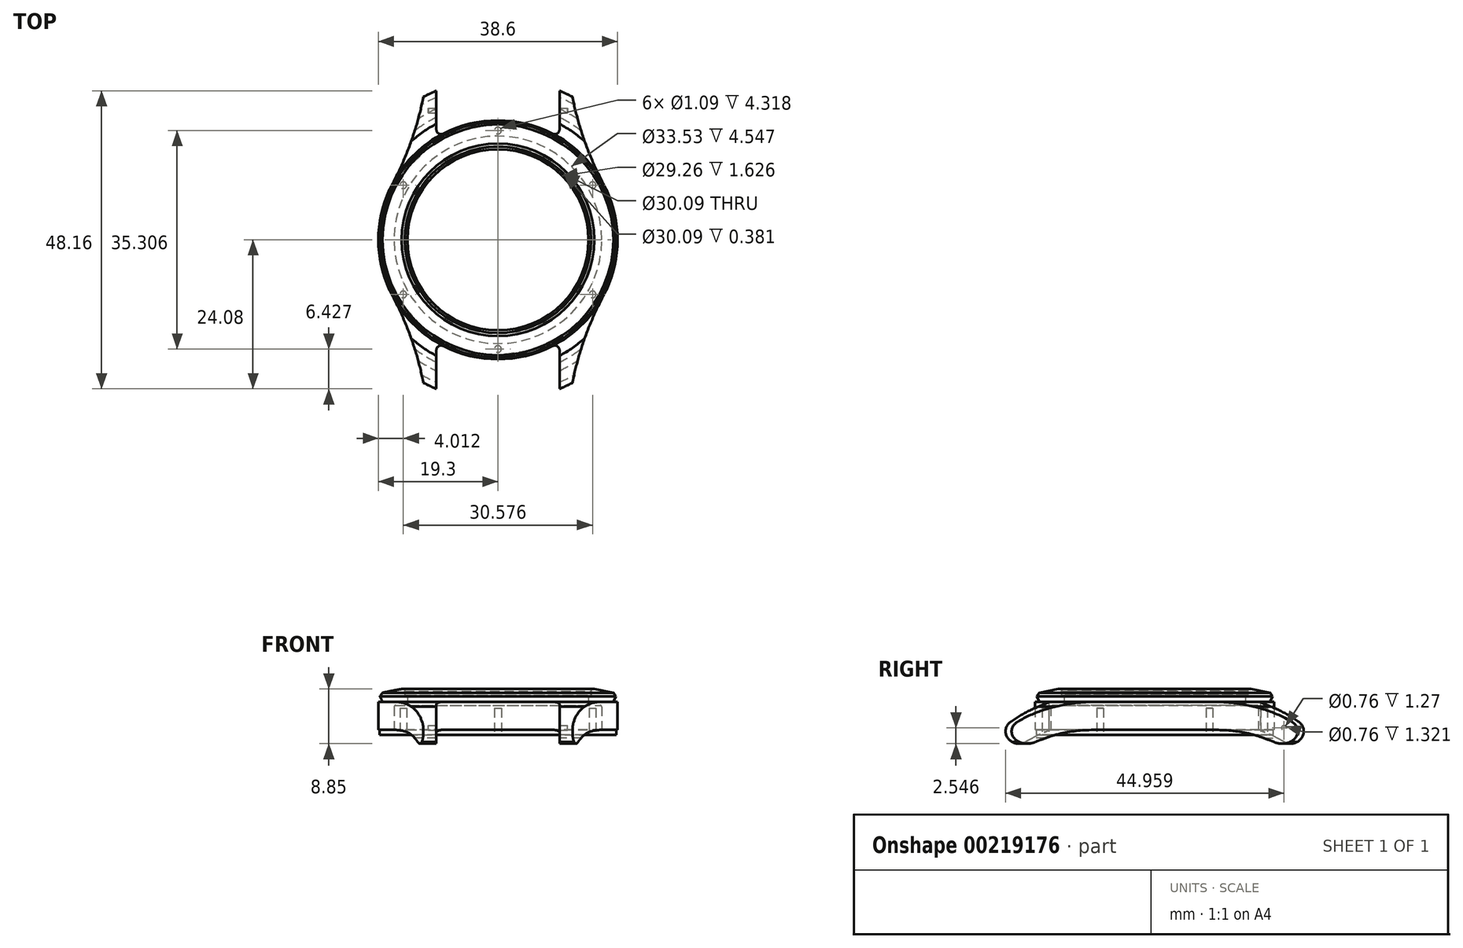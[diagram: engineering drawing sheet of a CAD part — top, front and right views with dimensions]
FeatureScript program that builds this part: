
annotation { "Feature Type Name" : "Feature", "Feature Type Description" : "" }
export const myFeature = defineFeature(function(context is Context, id is Id, definition is map)
    precondition{}
    {
        {
            var Q0;
            Q0=qCreatedBy(makeId("Front.planeOp"),FACE);
            var sketch = newSketch(context, id + "F0", { "sketchPlane" : qUnion([Q0])});
            skLineSegment(sketch, "E0", {"start": v(-19.1, -0.13) * mm, "end": v(-19.1, 0.58) * mm});
            skLineSegment(sketch, "E1", {"start": v(-19.23, 0.71) * mm, "end": v(-19.3, 0.71) * mm});
            skLineSegment(sketch, "E2", {"start": v(-19.3, 0.71) * mm, "end": v(-19.3, 5.23) * mm});
            skLineSegment(sketch, "E3", {"start": v(-14.77, 6.3) * mm, "end": v(-14.63, 6.3) * mm});
            skLineSegment(sketch, "E4", {"start": v(-14.63, 6.3) * mm, "end": v(-14.63, 4.67) * mm});
            skLineSegment(sketch, "E5", {"start": v(-16.76, -0.13) * mm, "end": v(-16.76, 4.42) * mm});
            skLineSegment(sketch, "E6", {"start": v(-16.5, 4.67) * mm, "end": v(-14.63, 4.67) * mm});
            skLineSegment(sketch, "E7", {"start": v(0, 0) * mm, "end": v(0, 7.56) * mm, "construction": true});
            skLineSegment(sketch, "E8", {"start": v(-19.3, 5.23) * mm, "end": v(-18.82, 5.23) * mm});
            skPoint(sketch, "E9.visualSharp", {"position": v(-16.76, 4.67) * mm});
            skArc(sketch, "E9.filletArc", {"start": v(-16.5, 4.67) * mm, "mid": v(-16.69, 4.6) * mm, "end": v(-16.76, 4.42) * mm});
            skPoint(sketch, "E10.visualSharp", {"position": v(-19.1, 0.71) * mm});
            skArc(sketch, "E10.filletArc", {"start": v(-19.1, 0.58) * mm, "mid": v(-19.14, 0.67) * mm, "end": v(-19.23, 0.71) * mm});
            skPoint(sketch, "E11.visualSharp", {"position": v(-15.17, 6.8) * mm});
            skLineSegment(sketch, "E12.0", {"start": v(-19.1, -0.13) * mm, "end": v(-16.76, -0.13) * mm});
            skLineSegment(sketch, "E13.0", {"start": v(-19.05, 6.13) * mm, "end": v(-18.7, 5.41) * mm});
            skArc(sketch, "E14.filletArc", {"start": v(-18.82, 5.23) * mm, "mid": v(-18.71, 5.3) * mm, "end": v(-18.7, 5.41) * mm});
            skPoint(sketch, "E15", {"position": v(-15.55, 7.32) * mm});
            skLineSegment(sketch, "E16", {"start": v(-15.55, 7.32) * mm, "end": v(-15.04, 7.32) * mm});
            skPoint(sketch, "E17", {"position": v(-18.64, 6.7) * mm});
            skLineSegment(sketch, "E18", {"start": v(-18.64, 6.7) * mm, "end": v(-15.55, 7.32) * mm});
            skPoint(sketch, "E19", {"position": v(-19.05, 6.13) * mm});
            skLineSegment(sketch, "E20", {"start": v(-18.64, 6.7) * mm, "end": v(-19.05, 6.13) * mm});
            skLineSegment(sketch, "E21", {"start": v(-14.77, 6.3) * mm, "end": v(-14.92, 6.3) * mm});
            skLineSegment(sketch, "E22", {"start": v(-15.04, 7.32) * mm, "end": v(-15.04, 6.93) * mm});
            skLineSegment(sketch, "E23", {"start": v(-15.04, 6.93) * mm, "end": v(-15.17, 6.8) * mm});
            skLineSegment(sketch, "E24", {"start": v(-15.17, 6.8) * mm, "end": v(-15.04, 6.68) * mm});
            skLineSegment(sketch, "E25.trimOffspring", {"start": v(-15.04, 6.68) * mm, "end": v(-15.04, 6.43) * mm});
            skArc(sketch, "E26.filletArc", {"start": v(-15.04, 6.43) * mm, "mid": v(-15, 6.34) * mm, "end": v(-14.92, 6.3) * mm});
            skSolve(sketch);
        }
        {
            var Q0;
            Q0=makeQuery(id+"F0.imprint","IMPRINT",FACE,{"disambiguationData":[TD([[makeQuery(id+"F0.imprint","IMPRINT",EDGE,{"derivedFrom":sQuery(id+"F0.wireOp",EDGE,"E0")}),-1.0]])]});
            var Q1;
            Q1=sQuery(id+"F0.wireOp",EDGE,"E7");
            revolve(context, id + "F1", {"entities" : qUnion([Q0]), "axis" : qUnion([Q1]), "revolveType" : RevolveType.FULL});
        }
        {
            var Q0;
            Q0=qCreatedBy(makeId("Front.planeOp"),FACE);
            var sketch = newSketch(context, id + "F2", { "sketchPlane" : qUnion([Q0])});
            skPoint(sketch, "E27.visualSharp", {"position": v(82.97, 5.54) * mm});
            skLineSegment(sketch, "E28", {"start": v(0, 0) * mm, "end": v(0, 14.04) * mm, "construction": true});
            skLineSegment(sketch, "E29", {"start": v(-19.3, 5.23) * mm, "end": v(-19.3, 0.71) * mm});
            skArc(sketch, "E30.filletArc", {"start": v(-25.06, -1.26) * mm, "mid": v(-24.23, -1.52) * mm, "end": v(-23.37, -1.36) * mm});
            skArc(sketch, "E31.trimOffspring", {"start": v(-25.5, 1.83) * mm, "mid": v(-26.03, 0.18) * mm, "end": v(-25.06, -1.26) * mm});
            skArc(sketch, "E32.trimOffspring", {"start": v(-22.16, -0.64) * mm, "mid": v(-22.77, -0.99) * mm, "end": v(-23.37, -1.36) * mm});
            skArc(sketch, "E33", {"start": v(-21.22, 4.48) * mm, "mid": v(-23.33, 3.36) * mm, "end": v(-25.3, 2.01) * mm});
            skArc(sketch, "E34.filletArc", {"start": v(-25.3, 2.01) * mm, "mid": v(-25.4, 1.92) * mm, "end": v(-25.5, 1.83) * mm});
            skArc(sketch, "E35", {"start": v(-19.3, 5.23) * mm, "mid": v(-20.28, 4.9) * mm, "end": v(-21.22, 4.48) * mm});
            skPoint(sketch, "E35.second.point", {"position": v(-21.22, 4.48) * mm});
            skArc(sketch, "E36", {"start": v(-19.3, 0.71) * mm, "mid": v(-20.78, 0.15) * mm, "end": v(-22.16, -0.64) * mm});
            skPoint(sketch, "E36.second.point", {"position": v(-22.16, -0.64) * mm});
            skLineSegment(sketch, "E37", {"start": v(-19.3, 5.23) * mm, "end": v(-29.9, 0.8) * mm});
            skSolve(sketch);
        }
        {
            var Q0;
            Q0 = qSketchRegion(id + "F2", true);
            var Q1;
            Q1=sQuery(id+"F2.wireOp",EDGE,"E28");
            revolve(context, id + "F3", {"operationType" : NewBodyOperationType.ADD, "entities" : qUnion([Q0]), "axis" : qUnion([Q1]), "revolveType" : RevolveType.FULL});
        }
        {
            var Q0;
            Q0=qCreatedBy(makeId("Top.planeOp"),FACE);
            var sketch = newSketch(context, id + "F4", { "sketchPlane" : qUnion([Q0])});
            skArc(sketch, "E38", {"start": v(8.83, 17.16) * mm, "mid": v(0, 19.3) * mm, "end": v(-8.83, 17.16) * mm});
            skCircle(sketch, "E39.converted", {"center": v(0, 0) * mm, "radius": 47.32 * mm});
            skLineSegment(sketch, "E40.MirrorCS", {"start": v(9.94, 29.16) * mm, "end": v(9.94, 17.84) * mm});
            skArc(sketch, "E41.trimOffspring", {"start": v(-17.5, 8.13) * mm, "mid": v(-19.3, 0) * mm, "end": v(-17.5, -8.13) * mm});
            skArc(sketch, "E42", {"start": v(11.21, 29.16) * mm, "mid": v(13.12, 18.67) * mm, "end": v(17.17, 8.81) * mm});
            skLineSegment(sketch, "E43", {"start": v(11.21, 29.16) * mm, "end": v(9.94, 29.16) * mm});
            skArc(sketch, "E44.filletArc", {"start": v(17.5, 8.13) * mm, "mid": v(17.34, 8.47) * mm, "end": v(17.17, 8.81) * mm});
            skLineSegment(sketch, "E45.MirrorCS", {"start": v(-9.94, 29.16) * mm, "end": v(-9.94, 17.84) * mm});
            skLineSegment(sketch, "E46.MirrorCS", {"start": v(-11.21, 29.16) * mm, "end": v(-9.94, 29.16) * mm});
            skArc(sketch, "E47.MirrorCS", {"start": v(-11.21, 29.16) * mm, "mid": v(-13.12, 18.67) * mm, "end": v(-17.17, 8.81) * mm});
            skArc(sketch, "E48.MirrorCS", {"start": v(-17.5, 8.13) * mm, "mid": v(-17.34, 8.47) * mm, "end": v(-17.17, 8.81) * mm});
            skArc(sketch, "E49.MirrorCS", {"start": v(-17.5, -8.13) * mm, "mid": v(-17.34, -8.47) * mm, "end": v(-17.17, -8.81) * mm});
            skArc(sketch, "E50.MirrorCS", {"start": v(-11.21, -29.16) * mm, "mid": v(-13.12, -18.67) * mm, "end": v(-17.17, -8.81) * mm});
            skLineSegment(sketch, "E51.MirrorCS", {"start": v(-11.21, -29.16) * mm, "end": v(-9.94, -29.16) * mm});
            skLineSegment(sketch, "E52.MirrorCS", {"start": v(-9.94, -29.16) * mm, "end": v(-9.94, -17.84) * mm});
            skLineSegment(sketch, "E53.MirrorCS", {"start": v(9.94, -29.16) * mm, "end": v(9.94, -17.84) * mm});
            skLineSegment(sketch, "E54.MirrorCS", {"start": v(11.21, -29.16) * mm, "end": v(9.94, -29.16) * mm});
            skArc(sketch, "E55.MirrorCS", {"start": v(11.21, -29.16) * mm, "mid": v(13.12, -18.67) * mm, "end": v(17.17, -8.81) * mm});
            skArc(sketch, "E56.MirrorCS", {"start": v(17.5, -8.13) * mm, "mid": v(17.34, -8.47) * mm, "end": v(17.17, -8.81) * mm});
            skArc(sketch, "E57.trimOffspring", {"start": v(-8.83, -17.16) * mm, "mid": v(0, -19.3) * mm, "end": v(8.83, -17.16) * mm});
            skArc(sketch, "E58.trimOffspring", {"start": v(17.5, -8.13) * mm, "mid": v(19.3, 0) * mm, "end": v(17.5, 8.13) * mm});
            skPoint(sketch, "E59.visualSharp", {"position": v(9.94, 16.55) * mm});
            skArc(sketch, "E59.filletArc", {"start": v(8.83, 17.16) * mm, "mid": v(9.58, 17.2) * mm, "end": v(9.94, 17.84) * mm});
            skPoint(sketch, "E60.visualSharp", {"position": v(-9.94, 16.55) * mm});
            skArc(sketch, "E60.filletArc", {"start": v(-9.94, 17.84) * mm, "mid": v(-9.58, 17.2) * mm, "end": v(-8.83, 17.16) * mm});
            skPoint(sketch, "E61.visualSharp", {"position": v(9.94, -16.55) * mm});
            skArc(sketch, "E61.filletArc", {"start": v(9.94, -17.84) * mm, "mid": v(9.58, -17.2) * mm, "end": v(8.83, -17.16) * mm});
            skPoint(sketch, "E62.visualSharp", {"position": v(-9.94, -16.55) * mm});
            skArc(sketch, "E63.filletArc", {"start": v(-8.83, -17.16) * mm, "mid": v(-9.58, -17.2) * mm, "end": v(-9.94, -17.84) * mm});
            skSolve(sketch);
        }
        {
            var Q0;
            Q0=makeQuery(id+"F4.imprint","IMPRINT",FACE,{"disambiguationData":[TD([[makeQuery(id+"F4.imprint","IMPRINT",EDGE,{"derivedFrom":sQuery(id+"F4.wireOp",EDGE,"E38")}),-1.0]])]});
            extrude(context, id + "F5", {"entities" : qUnion([Q0]), "operationType" : NewBodyOperationType.REMOVE, "depth" : 6.35 * mm, "hasSecondDirection" : true, "secondDirectionOppositeDirection" : true, "secondDirectionDepth" : 4.44 * mm});
        }
        {
            var Q0;
            Q0=makeQuery(id+"F1.opRevolve","SWEPT_FACE",FACE,{"disambiguationData":[OSD([sQuery(id+"F0.wireOp",EDGE,"E12.0")])]});
            var sketch = newSketch(context, id + "F6", { "sketchPlane" : qUnion([Q0])});
            skCircle(sketch, "E64", {"center": v(0, -17.65) * mm, "radius": 0.55 * mm});
            skCircle(sketch, "E65.1.0", {"center": v(15.29, -8.83) * mm, "radius": 0.55 * mm});
            skCircle(sketch, "E65.2.0", {"center": v(15.29, 8.83) * mm, "radius": 0.55 * mm});
            skPoint(sketch, "E65.center", {"position": v(0, 0) * mm});
            skCircle(sketch, "E66.1.3.0", {"center": v(0, 17.65) * mm, "radius": 0.55 * mm});
            skCircle(sketch, "E66.1.4.0", {"center": v(-15.29, 8.83) * mm, "radius": 0.55 * mm});
            skCircle(sketch, "E66.1.5.0", {"center": v(-15.29, -8.83) * mm, "radius": 0.55 * mm});
            skCircle(sketch, "E67", {"center": v(0, 0) * mm, "radius": 17.65 * mm, "construction": true});
            skSolve(sketch);
        }
        {
            var Q0;
            Q0 = qSketchRegion(id + "F6", true);
            var Q1;
            Q1 = qSketchRegion(id + "F8", true);
            extrude(context, id + "F7", {"entities" : qUnion([Q0, Q1]), "operationType" : NewBodyOperationType.REMOVE, "oppositeDirection" : true, "depth" : 4.32 * mm});
        }
        {
            var Q0;
            Q0=makeQuery(id+"F5.boolean.opBoolean","COPY",FACE,{"derivedFrom":makeQuery(id+"F5.opExtrude","SWEPT_FACE",FACE,{"disambiguationData":[OSD([sQuery(id+"F4.wireOp",EDGE,"E45.MirrorCS")])]})});
            var sketch = newSketch(context, id + "F8", { "sketchPlane" : qUnion([Q0])});
            skCircle(sketch, "E68", {"center": v(20.88, 1.02) * mm, "radius": 0.38 * mm});
            skCircle(sketch, "E69.MirrorC", {"center": v(-20.88, 1.02) * mm, "radius": 0.38 * mm});
            skSolve(sketch);
        }
        {
            var Q0;
            Q0=makeQuery(id+"F8.imprint","IMPRINT",FACE,{"disambiguationData":[TD([[makeQuery(id+"F8.imprint","IMPRINT",EDGE,{"derivedFrom":sQuery(id+"F8.wireOp",EDGE,"E68")}),1.0]])]});
            var Q1;
            Q1=makeQuery(id+"F8.imprint","IMPRINT",FACE,{"disambiguationData":[TD([[makeQuery(id+"F8.imprint","IMPRINT",EDGE,{"derivedFrom":sQuery(id+"F8.wireOp",EDGE,"E69.MirrorC")}),-1.0]])]});
            var Q2;
            Q2=makeQuery(id+"F5.boolean.opBoolean","COPY",FACE,{"derivedFrom":makeQuery(id+"F5.opExtrude","SWEPT_FACE",FACE,{"disambiguationData":[OSD([sQuery(id+"F4.wireOp",EDGE,"E40.MirrorCS")])]})});
            extrude(context, id + "F9", {"entities" : qUnion([Q0, Q1]), "operationType" : NewBodyOperationType.REMOVE, "oppositeDirection" : true, "endBoundEntityFace" : qUnion([Q2]), "depth" : 1.27 * mm, "hasSecondDirection" : true, "secondDirectionOppositeDirection" : false, "secondDirectionDepth" : 21.2 * mm});
        }
    });
